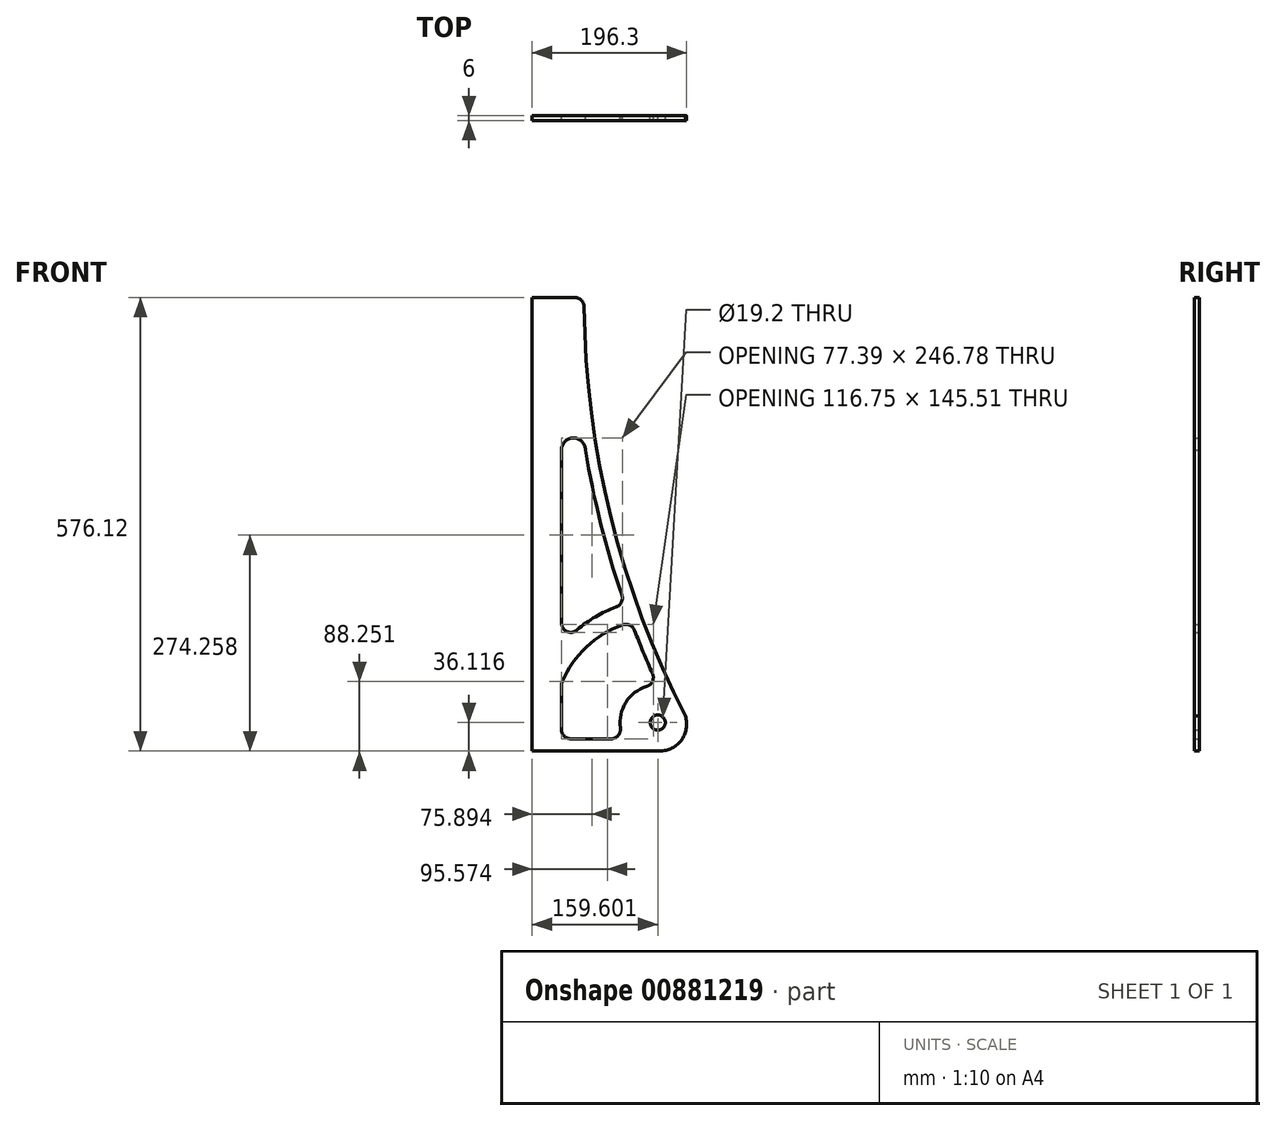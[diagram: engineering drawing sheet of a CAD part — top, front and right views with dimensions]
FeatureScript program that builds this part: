
annotation { "Feature Type Name" : "Feature", "Feature Type Description" : "" }
export const myFeature = defineFeature(function(context is Context, id is Id, definition is map)
    precondition{}
    {
        {
            var Q0;
            Q0=qCreatedBy(makeId("Front.planeOp"),FACE);
            var sketch = newSketch(context, id + "F0", { "sketchPlane" : qUnion([Q0])});
            skLineSegment(sketch, "E0", {"start": v(-98.15, -287.94) * mm, "end": v(-98.15, 288.06) * mm});
            skLineSegment(sketch, "E1", {"start": v(-98.15, 288.06) * mm, "end": v(-44.09, 288.06) * mm});
            skArc(sketch, "E2", {"start": v(-32.09, 276.18) * mm, "mid": v(-35.65, 284.58) * mm, "end": v(-44.09, 288.06) * mm});
            skArc(sketch, "E3", {"start": v(-32.09, 276.18) * mm, "mid": v(1.87, 8.85) * mm, "end": v(96.44, -243.48) * mm});
            skArc(sketch, "E4", {"start": v(-30.5, 94.37) * mm, "mid": v(-45.73, 109.59) * mm, "end": v(-60.95, 94.37) * mm});
            skLineSegment(sketch, "E5", {"start": v(-60.95, -125.31) * mm, "end": v(-60.95, 94.37) * mm});
            skArc(sketch, "E6", {"start": v(-31.3, 99.25) * mm, "mid": v(-11.67, 3.62) * mm, "end": v(15.82, -90.05) * mm});
            skArc(sketch, "E7", {"start": v(15.82, -90.05) * mm, "mid": v(15.27, -99.11) * mm, "end": v(8.53, -105.2) * mm});
            skArc(sketch, "E8", {"start": v(8.53, -105.2) * mm, "mid": v(-17.62, -117.47) * mm, "end": v(-41.06, -134.36) * mm});
            skArc(sketch, "E9", {"start": v(-60.95, -125.31) * mm, "mid": v(-53.92, -136.23) * mm, "end": v(-41.06, -134.36) * mm});
            skArc(sketch, "E10", {"start": v(16.72, -127.75) * mm, "mid": v(-29.19, -155.98) * mm, "end": v(-59.99, -200.21) * mm});
            skArc(sketch, "E11", {"start": v(16.72, -127.75) * mm, "mid": v(25.78, -128.13) * mm, "end": v(31.99, -134.73) * mm});
            skArc(sketch, "E12", {"start": v(31.99, -134.73) * mm, "mid": v(43.03, -162.38) * mm, "end": v(54.76, -189.73) * mm});
            skArc(sketch, "E13", {"start": v(54.76, -189.73) * mm, "mid": v(54.72, -199.57) * mm, "end": v(47.33, -206.07) * mm});
            skArc(sketch, "E14", {"start": v(47.33, -206.07) * mm, "mid": v(20.89, -226.29) * mm, "end": v(13.95, -258.84) * mm});
            skArc(sketch, "E15", {"start": v(2.07, -272.56) * mm, "mid": v(11.15, -268.42) * mm, "end": v(13.95, -258.84) * mm});
            skLineSegment(sketch, "E16", {"start": v(2.07, -272.56) * mm, "end": v(-48.95, -272.56) * mm});
            skLineSegment(sketch, "E17", {"start": v(-60.95, -260.56) * mm, "end": v(-60.95, -204.91) * mm});
            skArc(sketch, "E18", {"start": v(-60.95, -260.56) * mm, "mid": v(-57.43, -269.05) * mm, "end": v(-48.95, -272.56) * mm});
            skLineSegment(sketch, "E19", {"start": v(61.45, -287.94) * mm, "end": v(-98.15, -287.94) * mm});
            skArc(sketch, "E20", {"start": v(61.45, -287.94) * mm, "mid": v(90.88, -275.1) * mm, "end": v(96.44, -243.48) * mm});
            skArc(sketch, "E21", {"start": v(-59.99, -200.21) * mm, "mid": v(-60.7, -202.51) * mm, "end": v(-60.95, -204.91) * mm});
            skCircle(sketch, "E22", {"center": v(61.45, -251.94) * mm, "radius": 9.6 * mm});
            skSolve(sketch);
        }
        {
            var Q0;
            Q0=makeQuery(id+"F0.imprint","IMPRINT",FACE,{"disambiguationData":[TD([[makeQuery(id+"F0.imprint","IMPRINT",EDGE,{"derivedFrom":sQuery(id+"F0.wireOp",EDGE,"E0")}),-1.0]])]});
            extrude(context, id + "F1", {"entities" : qUnion([Q0]), "depth" : 6 * mm, "offsetDistance" : 25 * mm});
        }
    });
